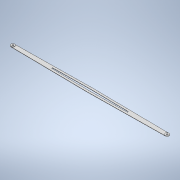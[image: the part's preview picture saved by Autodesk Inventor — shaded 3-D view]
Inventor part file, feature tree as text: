
AUTODESK INVENTOR PART (.ipt)
format: ipt  version: 2020 (Build 240168000, 168)  size: 133,120 bytes
history: native  units: mm
features: extrude x2, sketch x1, fillet x1
ambient origin geometry x8: Origin, YZ Plane, XZ Plane, XY Plane, X Axis, Y Axis, Z Axis, Center Point
bodies: Solid1 (feature_tree)
feature tree (4):
  sketch  "Sketch1"  dims[d0=15.0mm d1=5.5mm d2=294.76mm d3=8.0mm d4=23.0mm d5=1.0mm d6=0.0mm d7=2.0mm d8=0.0mm d9=2.0mm]
  extrude  "Extrusion1"  Depth=2.0mm
  extrude  "Extrusion2"  Depth=294.76mm
  fillet  "Fillet1"  Radius=8.0mm
